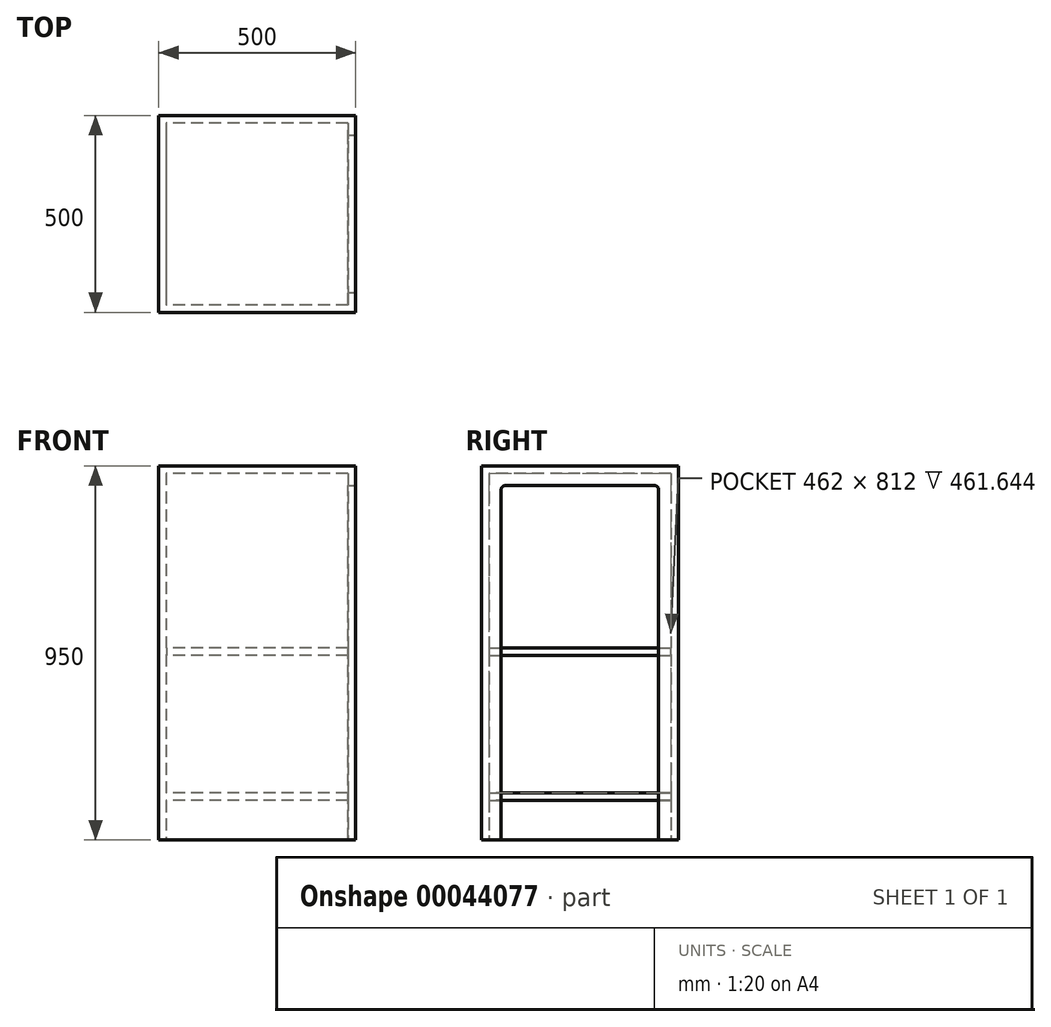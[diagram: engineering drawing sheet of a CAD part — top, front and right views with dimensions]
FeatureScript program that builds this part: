
annotation { "Feature Type Name" : "Feature", "Feature Type Description" : "" }
export const myFeature = defineFeature(function(context is Context, id is Id, definition is map)
    precondition{}
    {
        {
            var Q0;
            Q0=qCreatedBy(makeId("Top.planeOp"),FACE);
            var sketch = newSketch(context, id + "F0", { "sketchPlane" : qUnion([Q0])});
            skLineSegment(sketch, "E0.rect.bottom", {"start": v(250, 250) * mm, "end": v(-250, 250) * mm});
            skLineSegment(sketch, "E0.rect.top", {"start": v(250, -250) * mm, "end": v(-250, -250) * mm});
            skLineSegment(sketch, "E0.rect.left", {"start": v(250, 250) * mm, "end": v(250, -250) * mm});
            skLineSegment(sketch, "E0.rect.right", {"start": v(-250, 250) * mm, "end": v(-250, -250) * mm});
            skPoint(sketch, "E0.rect.middle", {"position": v(0, 0) * mm});
            skSolve(sketch);
        }
        {
            var Q0;
            Q0 = qSketchRegion(id + "F0", true);
            extrude(context, id + "F1", {"entities" : qUnion([Q0]), "depth" : 950 * mm});
        }
        {
            var Q0;
            Q0=makeQuery(id+"F1.opExtrude","CAP_FACE",FACE,{"disambiguationData":[OSD([sQuery(id+"F0.wireOp",EDGE,"E0.rect.bottom"),sQuery(id+"F0.wireOp",EDGE,"E0.rect.top"),sQuery(id+"F0.wireOp",EDGE,"E0.rect.left"),sQuery(id+"F0.wireOp",EDGE,"E0.rect.right")])],"isStart":true});
            shell(context, id + "F2", {"entities" : qUnion([Q0]), "thickness" : 19 * mm});
        }
        {
            var Q0;
            Q0=makeQuery(id+"F1.opExtrude","SWEPT_FACE",FACE,{"disambiguationData":[OSD([sQuery(id+"F0.wireOp",EDGE,"E0.rect.left")])]});
            var sketch = newSketch(context, id + "F3", { "sketchPlane" : qUnion([Q0])});
            skLineSegment(sketch, "E1.bottom", {"start": v(-200, 0) * mm, "end": v(200, 0) * mm});
            skLineSegment(sketch, "E1.top", {"start": v(-200, 900) * mm, "end": v(200, 900) * mm});
            skLineSegment(sketch, "E1.left", {"start": v(-200, 0) * mm, "end": v(-200, 900) * mm});
            skLineSegment(sketch, "E1.right", {"start": v(200, 0) * mm, "end": v(200, 900) * mm});
            skSolve(sketch);
        }
        {
            var Q0;
            Q0 = qSketchRegion(id + "F3", true);
            extrude(context, id + "F4", {"entities" : qUnion([Q0]), "operationType" : NewBodyOperationType.REMOVE, "oppositeDirection" : true, "depth" : 25 * mm});
        }
        {
            var Q0;
            Q0=makeQuery(id+"F4.boolean.opBoolean","COPY",EDGE,{"derivedFrom":makeQuery(id+"F4.opExtrude","SWEPT_EDGE",EDGE,{"disambiguationData":[OSD([sQuery(id+"F3.wireOp",EDGE,"E1.top"),sQuery(id+"F3.wireOp",EDGE,"E1.right")])]})});
            var Q1;
            Q1=makeQuery(id+"F4.boolean.opBoolean","COPY",EDGE,{"derivedFrom":makeQuery(id+"F4.opExtrude","SWEPT_EDGE",EDGE,{"disambiguationData":[OSD([sQuery(id+"F3.wireOp",EDGE,"E1.top"),sQuery(id+"F3.wireOp",EDGE,"E1.left")])]})});
            fillet(context, id + "F5", {"entities" : qUnion([Q0, Q1]), "radius" : 10 * mm, "tangentPropagation" : true, "allowEdgeOverflow" : false});
        }
        {
            var Q0;
            Q0=qCreatedBy(makeId("Top.planeOp"),FACE);
            cPlane(context, id + "F6", {"entities" : qUnion([Q0]), "cplaneType" : CPlaneType.OFFSET, "offset" : 100 * mm, "width" : 150 * mm, "height" : 150 * mm});
        }
        {
            var Q0;
            Q0=qCreatedBy(id+"F6.planeOp",FACE);
            var sketch = newSketch(context, id + "F7", { "sketchPlane" : qUnion([Q0])});
            skLineSegment(sketch, "E2.bottom", {"start": v(230.64, -231.06) * mm, "end": v(-231.06, -231.06) * mm});
            skLineSegment(sketch, "E2.top", {"start": v(230.64, 231.47) * mm, "end": v(-231.06, 231.47) * mm});
            skLineSegment(sketch, "E2.left", {"start": v(230.64, -231.06) * mm, "end": v(230.64, 231.47) * mm});
            skLineSegment(sketch, "E2.right", {"start": v(-231.06, -231.06) * mm, "end": v(-231.06, 231.47) * mm});
            skSolve(sketch);
        }
        {
            var Q0;
            Q0 = qSketchRegion(id + "F7", true);
            extrude(context, id + "F8", {"entities" : qUnion([Q0]), "operationType" : NewBodyOperationType.ADD, "depth" : 19 * mm});
        }
        {
            var Q0;
            Q0=makeQuery(id+"F8.opExtrude","CAP_FACE",FACE,{"disambiguationData":[OSD([sQuery(id+"F7.wireOp",EDGE,"E2.bottom"),sQuery(id+"F7.wireOp",EDGE,"E2.top"),sQuery(id+"F7.wireOp",EDGE,"E2.left"),sQuery(id+"F7.wireOp",EDGE,"E2.right")])],"isStart":false});
            cPlane(context, id + "F9", {"entities" : qUnion([Q0]), "cplaneType" : CPlaneType.OFFSET, "offset" : 350 * mm, "width" : 150 * mm, "height" : 150 * mm});
        }
        {
            var Q0;
            Q0=qCreatedBy(id+"F9.planeOp",FACE);
            var sketch = newSketch(context, id + "F10", { "sketchPlane" : qUnion([Q0])});
            skLineSegment(sketch, "E3.bottom", {"start": v(230.5, -231.06) * mm, "end": v(-230.28, -231.06) * mm});
            skLineSegment(sketch, "E3.top", {"start": v(230.5, 230.61) * mm, "end": v(-230.28, 230.61) * mm});
            skLineSegment(sketch, "E3.left", {"start": v(230.5, -231.06) * mm, "end": v(230.5, 230.61) * mm});
            skLineSegment(sketch, "E3.right", {"start": v(-230.28, -231.06) * mm, "end": v(-230.28, 230.61) * mm});
            skSolve(sketch);
        }
        {
            var Q0;
            Q0 = qSketchRegion(id + "F10", true);
            extrude(context, id + "F11", {"entities" : qUnion([Q0]), "operationType" : NewBodyOperationType.ADD, "depth" : 19 * mm});
        }
    });
